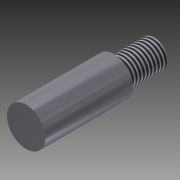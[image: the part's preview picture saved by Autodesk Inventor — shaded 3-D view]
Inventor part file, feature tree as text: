
AUTODESK INVENTOR PART (.ipt)
format: ipt  version: 2012 (Build 160160000, 160)  size: 94,208 bytes
history: native  units: in
note: dims shown in document units (in); Inventor stores cm internally (conversion verified against a paired STEP export)
features: extrude x3, sketch x2, thread x2
ambient origin geometry x8: Origin, YZ Plane, XZ Plane, XY Plane, X Axis, Y Axis, Z Axis, Center Point
bodies: Solid1 (feature_tree)
feature tree (7):
  sketch  "Sketch1"  dims[d0=0.525in d1=0.375in]
  extrude  "Extrusion1"  Depth=0.375in
  extrude  "Extrusion2"  Depth=1.2in TaperAngle=0.0deg
  thread  "Thread1"  [1 undecoded]
  extrude  "Extrusion3"  Depth=0.19in
  thread  "Thread2"  [1 undecoded]
  sketch  "Sketch2"  dims[d2=0.546in d3=0.0in d4=1.2in d5=0.0in d6=1.0in d7=0.0in d8=0.19in d9=1.0in d10=0.0in d11=1.0in d12=0.0in]
note: 2 required parameter values undecoded (feature->parameter linkage not recoverable at this tier; creation-order binding heuristic only, values carry confidence <= 0.55)
